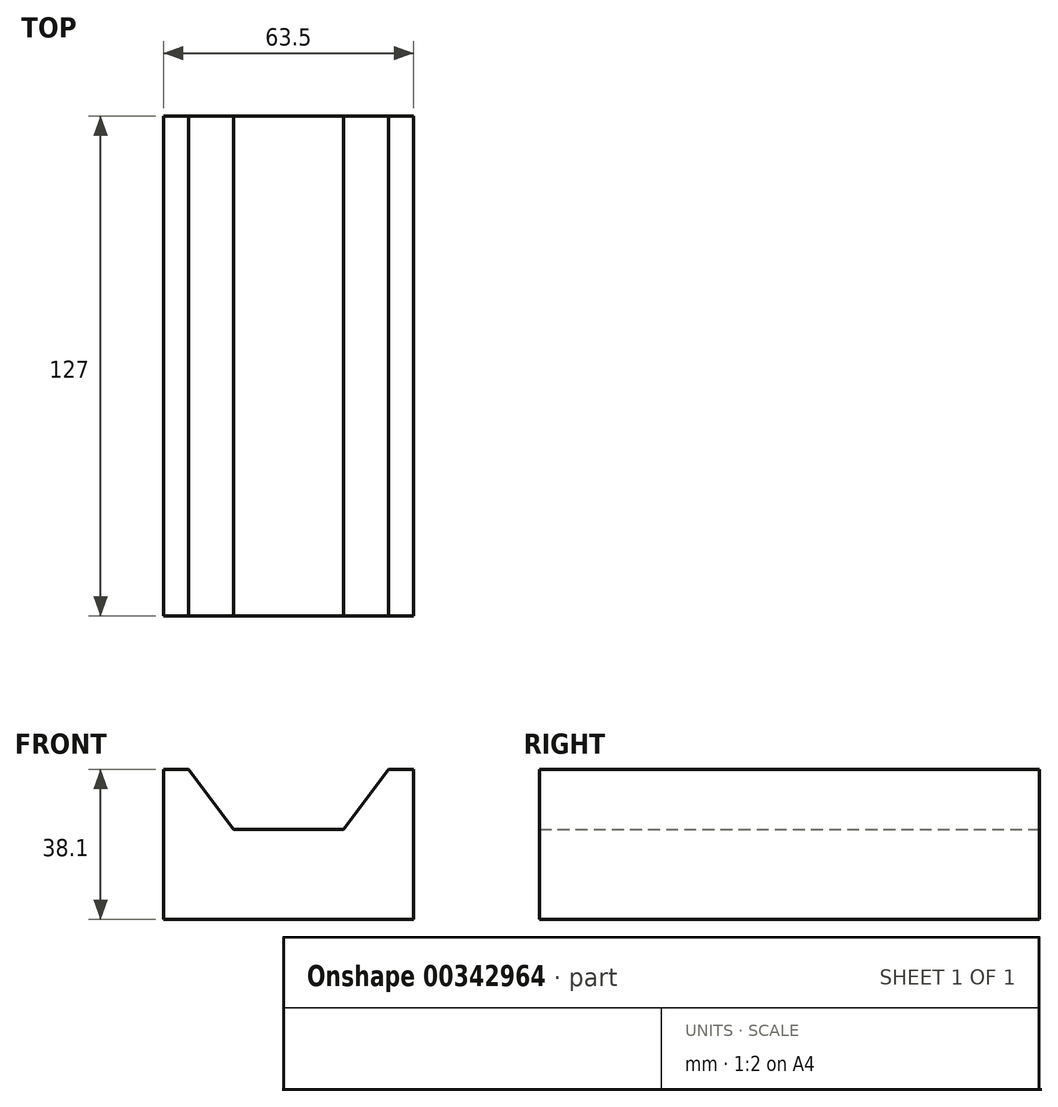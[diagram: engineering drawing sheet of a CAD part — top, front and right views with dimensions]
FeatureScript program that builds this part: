
annotation { "Feature Type Name" : "Feature", "Feature Type Description" : "" }
export const myFeature = defineFeature(function(context is Context, id is Id, definition is map)
    precondition{}
    {
        {
            var Q0;
            Q0=qCreatedBy(makeId("Front.planeOp"),FACE);
            var sketch = newSketch(context, id + "F0", { "sketchPlane" : qUnion([Q0])});
            skLineSegment(sketch, "E0", {"start": v(-27.09, -38.1) * mm, "end": v(36.41, -38.1) * mm});
            skLineSegment(sketch, "E1", {"start": v(-27.09, -38.1) * mm, "end": v(-27.09, 0) * mm});
            skLineSegment(sketch, "E2", {"start": v(36.41, -38.1) * mm, "end": v(36.41, 0) * mm});
            skLineSegment(sketch, "E3", {"start": v(-27.09, 0) * mm, "end": v(-20.74, 0) * mm});
            skLineSegment(sketch, "E4", {"start": v(36.41, 0) * mm, "end": v(30.06, 0) * mm});
            skLineSegment(sketch, "E5", {"start": v(-20.74, 0) * mm, "end": v(-9.33, -15.26) * mm});
            skLineSegment(sketch, "E6", {"start": v(30.06, 0) * mm, "end": v(18.66, -15.26) * mm});
            skLineSegment(sketch, "E7", {"start": v(-9.33, -15.26) * mm, "end": v(18.66, -15.26) * mm});
            skSolve(sketch);
        }
        {
            var Q0;
            Q0 = qSketchRegion(id + "F0", true);
            extrude(context, id + "F1", {"entities" : qUnion([Q0]), "depth" : 127 * mm});
        }
    });
